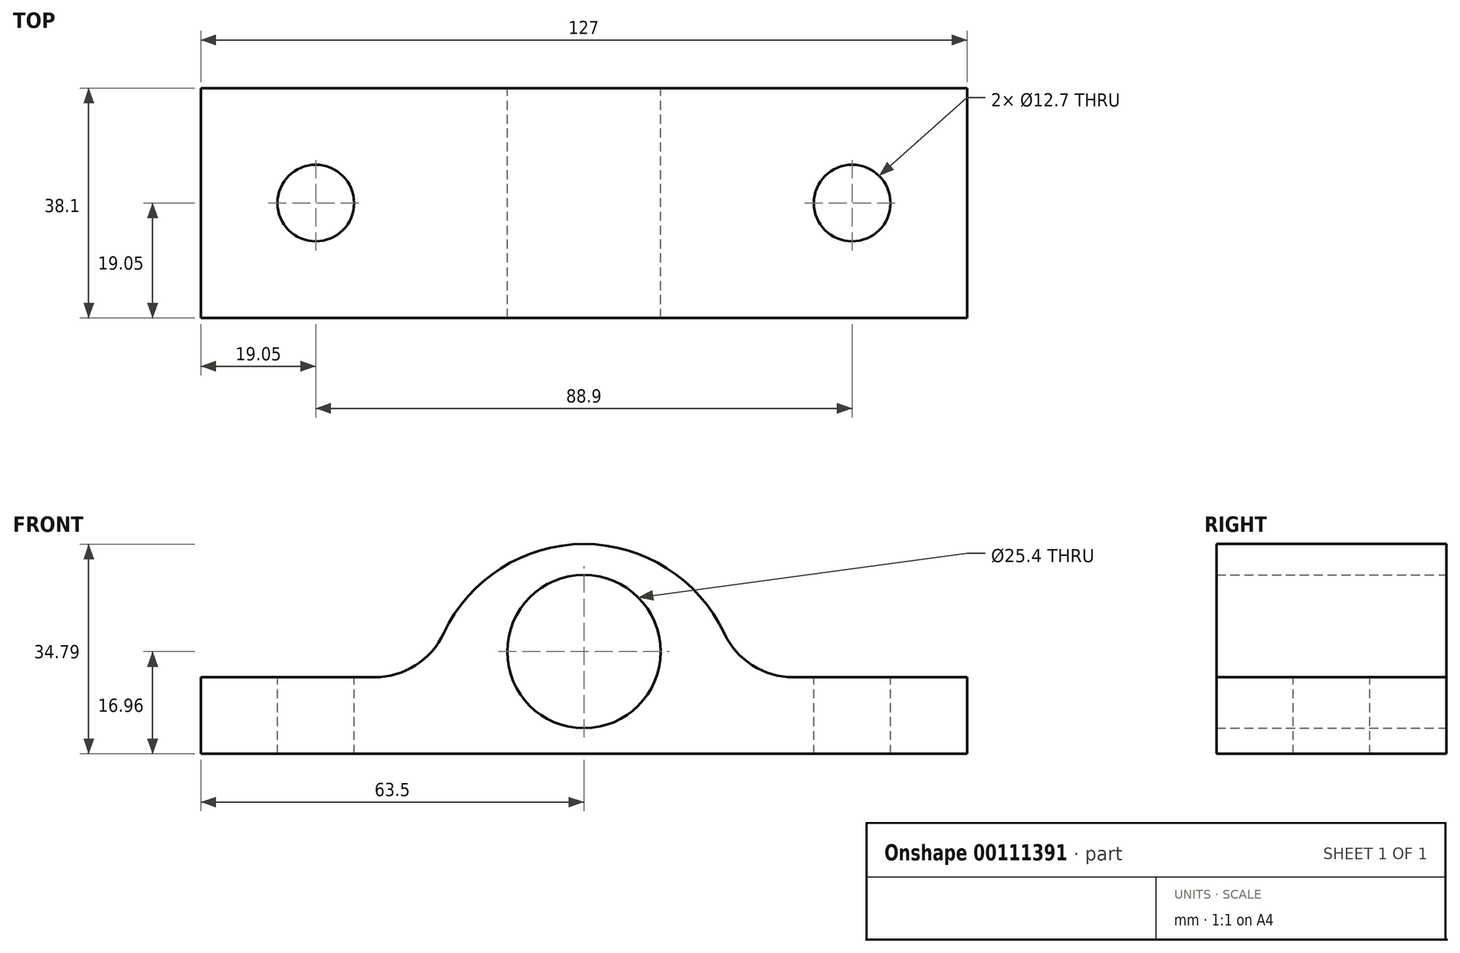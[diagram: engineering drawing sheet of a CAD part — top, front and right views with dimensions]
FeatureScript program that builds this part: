
annotation { "Feature Type Name" : "Feature", "Feature Type Description" : "" }
export const myFeature = defineFeature(function(context is Context, id is Id, definition is map)
    precondition{}
    {
        {
            var Q0;
            Q0=qCreatedBy(makeId("Front.planeOp"),FACE);
            var sketch = newSketch(context, id + "F0", { "sketchPlane" : qUnion([Q0])});
            skLineSegment(sketch, "E0", {"start": v(-63.5, 0) * mm, "end": v(63.5, 0) * mm});
            skLineSegment(sketch, "E1", {"start": v(-63.5, 0) * mm, "end": v(-63.5, 12.7) * mm});
            skLineSegment(sketch, "E2", {"start": v(-63.5, 12.7) * mm, "end": v(-34.73, 12.7) * mm});
            skLineSegment(sketch, "E3", {"start": v(34.73, 12.7) * mm, "end": v(63.5, 12.7) * mm});
            skLineSegment(sketch, "E4", {"start": v(63.5, 12.7) * mm, "end": v(63.5, 0) * mm});
            skCircle(sketch, "E5", {"center": v(0, 16.96) * mm, "radius": 12.7 * mm});
            skArc(sketch, "E6", {"start": v(23.23, 20.02) * mm, "mid": v(0, 34.8) * mm, "end": v(-23.23, 20.02) * mm});
            skPoint(sketch, "E7.visualSharp", {"position": v(-25.4, 12.7) * mm});
            skArc(sketch, "E7.filletArc", {"start": v(-34.73, 12.7) * mm, "mid": v(-27.92, 14.68) * mm, "end": v(-23.23, 20.02) * mm});
            skPoint(sketch, "E8.visualSharp", {"position": v(25.4, 12.7) * mm});
            skArc(sketch, "E8.filletArc", {"start": v(23.23, 20.02) * mm, "mid": v(27.92, 14.68) * mm, "end": v(34.73, 12.7) * mm});
            skSolve(sketch);
        }
        {
            var Q0;
            Q0 = qSketchRegion(id + "F0", true);
            extrude(context, id + "F1", {"entities" : qUnion([Q0]), "endBound" : BoundingType.SYMMETRIC, "depth" : 38.1 * mm});
        }
        {
            var Q0;
            Q0=qCreatedBy(makeId("Top.planeOp"),FACE);
            var sketch = newSketch(context, id + "F2", { "sketchPlane" : qUnion([Q0])});
            skCircle(sketch, "E9", {"center": v(44.45, 0) * mm, "radius": 6.35 * mm});
            skCircle(sketch, "E10", {"center": v(-44.45, 0) * mm, "radius": 6.35 * mm});
            skSolve(sketch);
        }
        {
            var Q0;
            Q0 = qSketchRegion(id + "F2", true);
            extrude(context, id + "F3", {"entities" : qUnion([Q0]), "operationType" : NewBodyOperationType.REMOVE, "endBound" : BoundingType.SYMMETRIC, "oppositeDirection" : true, "depth" : 25.4 * mm});
        }
    });
